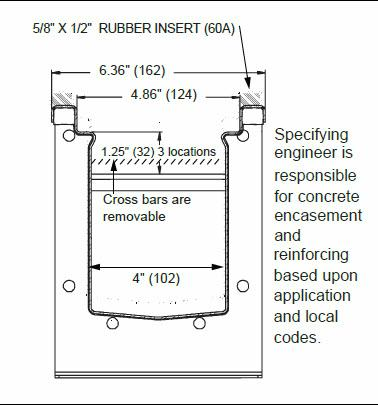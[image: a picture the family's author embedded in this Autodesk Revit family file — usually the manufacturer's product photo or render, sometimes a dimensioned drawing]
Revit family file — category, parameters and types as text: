
# Revit family: P6030
name_source: partatom
category: Plumbing Fixtures
revit_build: Autodesk Revit 2018 (Build: 20170223_1515(x64)
units: mm (PartAtom-declared; Revit-internal decimal feet)

## family parameters
Cut with Voids When Loaded = No
Host = Face
Part Type = Normal
Room Calculation Point = No
Round Connector Dimension = Use Diameter
Shared = No

## types (17) — shared parameters
Default Elevation = 48.00"
Description = 3" WIDE, 2" INTERNAL WIDTH STAINLESS STEEL CHANNEL AND GRATE SYSTEM
Manufacturer = MIFAB
Material = Paint - Sherwin Williams Paint - #952C2A - Bellwood Red
URL = WWW.MIFAB.COM

## per-type parameters (varying)
| type | C1 (Shallow Invert) | End Dim. | Length |
| P6031-PB | 3.00" | 11.90" | 78.74" |
| P6031N-PB | 3.78" | 11.90" | 78.74" |
| P6031N-PB-B02 | 3.78" | 11.90" | 78.74" |
| P6031N-PB-B03 | 3.78" | 11.90" | 78.74" |
| P6031N-PB-1M | 3.78" | 6.00" | 39.37" |
| P6032-PB | 3.78" | 11.90" | 78.74" |
| P6033-PB | 4.75" | 11.90" | 78.74" |
| P6033N-PB | 5.36" | 11.90" | 78.74" |
| P6033N-PB-B02 | 5.36" | 11.90" | 78.74" |
| P6033N-PB-B03 | 5.36" | 11.90" | 78.74" |
| P6033N-PB-1M | 5.36" | 6.00" | 39.37" |
| P6034-PB | 5.36" | 11.90" | 78.74" |
| P6035-PB | 6.15" | 11.90" | 78.74" |
| P6035N-PB | 6.94" | 11.90" | 78.74" |
| P6035N-PB-B02 | 6.94" | 11.90" | 78.74" |
| P6035N-PB-B03 | 6.94" | 11.90" | 78.74" |
| P6035N-PB-1M | 6.94" | 6.00" | 39.37" |

note: column(s) folded — value = type name in every type: Model

## geometry (parser evidence)
native form markers: Sweep x5
no freeform markers — native parametric forms only
